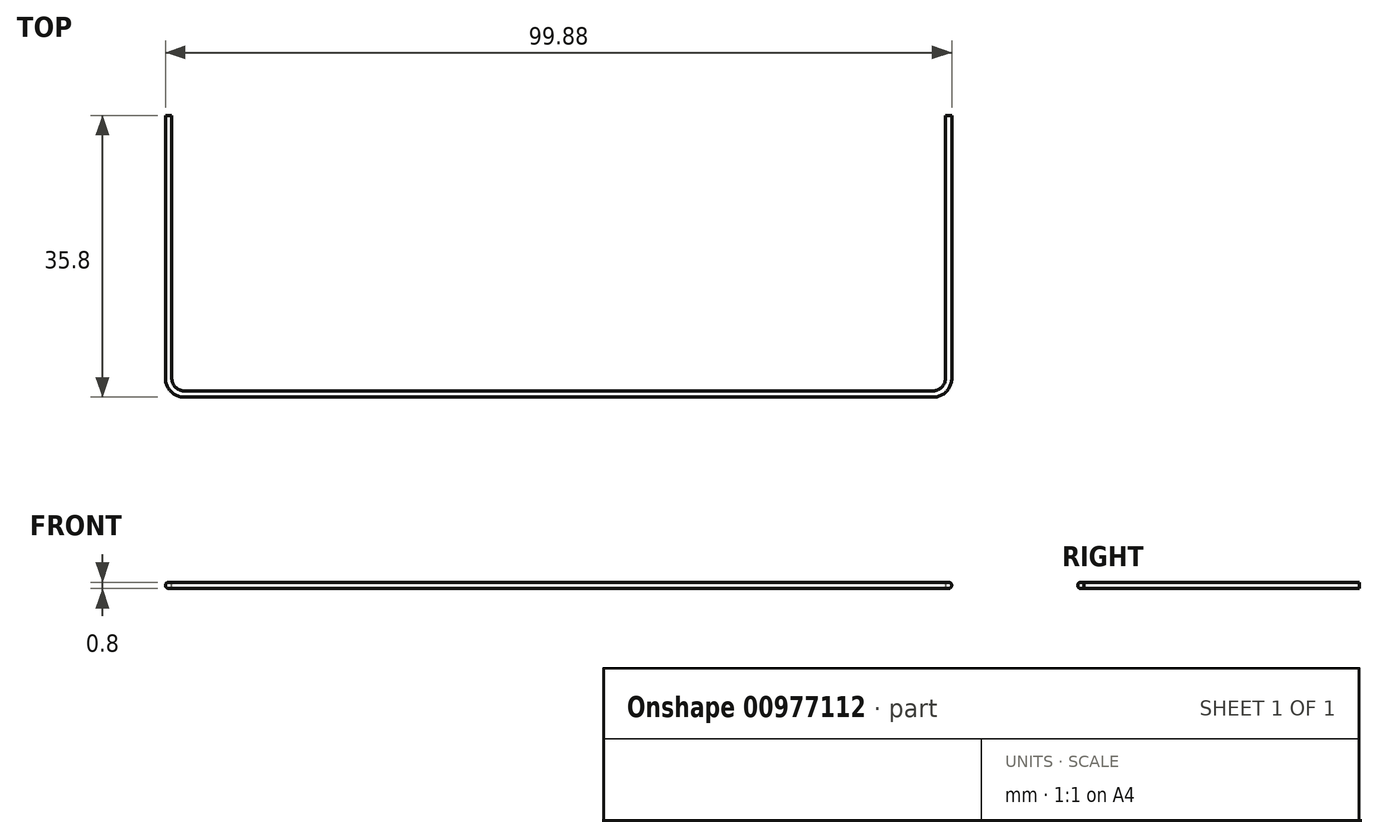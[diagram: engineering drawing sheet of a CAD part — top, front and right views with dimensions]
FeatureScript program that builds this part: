
annotation { "Feature Type Name" : "Feature", "Feature Type Description" : "" }
export const myFeature = defineFeature(function(context is Context, id is Id, definition is map)
    precondition{}
    {
        {
            var Q0;
            Q0=qCreatedBy(makeId("Top.planeOp"),FACE);
            var sketch = newSketch(context, id + "F0", { "sketchPlane" : qUnion([Q0])});
            skLineSegment(sketch, "E0", {"start": v(0, 30.38) * mm, "end": v(0, -52.81) * mm, "construction": true});
            skLineSegment(sketch, "E1", {"start": v(-78.63, 0) * mm, "end": v(95.22, 0) * mm, "construction": true});
            skLineSegment(sketch, "E2", {"start": v(0, 0) * mm, "end": v(0, -33.4) * mm});
            skLineSegment(sketch, "E3", {"start": v(2, -35.4) * mm, "end": v(97.08, -35.4) * mm});
            skLineSegment(sketch, "E4", {"start": v(99.08, -33.4) * mm, "end": v(99.08, 0) * mm});
            skPoint(sketch, "E5.visualSharp", {"position": v(0, -35.4) * mm});
            skArc(sketch, "E5.filletArc", {"start": v(0, -33.4) * mm, "mid": v(0.59, -34.81) * mm, "end": v(2, -35.4) * mm});
            skPoint(sketch, "E6.visualSharp", {"position": v(99.08, -35.4) * mm});
            skArc(sketch, "E6.filletArc", {"start": v(97.08, -35.4) * mm, "mid": v(98.5, -34.81) * mm, "end": v(99.08, -33.4) * mm});
            skSolve(sketch);
        }
        {
            var Q0;
            Q0=qCreatedBy(makeId("Front.planeOp"),FACE);
            var sketch = newSketch(context, id + "F1", { "sketchPlane" : qUnion([Q0])});
            skCircle(sketch, "E7", {"center": v(0, 0) * mm, "radius": 0.4 * mm});
            skSolve(sketch);
        }
        {
            var Q0;
            Q0=makeQuery(id+"F1.imprint","IMPRINT",FACE,{"disambiguationData":[TD([[makeQuery(id+"F1.imprint","IMPRINT",EDGE,{"derivedFrom":sQuery(id+"F1.wireOp",EDGE,"E7")}),1.0]])]});
            var Q1;
            Q1=sQuery(id+"F0.wireOp",EDGE,"E2");
            var Q2;
            Q2=sQuery(id+"F0.wireOp",EDGE,"E5.filletArc");
            var Q3;
            Q3=sQuery(id+"F0.wireOp",EDGE,"E3");
            var Q4;
            Q4=sQuery(id+"F0.wireOp",EDGE,"E6.filletArc");
            var Q5;
            Q5=sQuery(id+"F0.wireOp",EDGE,"E4");
            sweep(context, id + "F2", {"profiles" : qUnion([Q0]), "path" : qUnion([Q1, Q2, Q3, Q4, Q5])});
        }
    });
